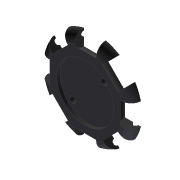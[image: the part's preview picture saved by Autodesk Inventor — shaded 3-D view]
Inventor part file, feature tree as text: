
AUTODESK INVENTOR PART (.ipt)
format: ipt  version: 2017 (Build 210142000, 142)  size: 216,576 bytes
history: native  units: mm
features: sketch x4, extrude x3, revolve x1, fillet x1, pattern_circular x1, hole x1, projected_geometry x1
ambient origin geometry x8: Origin, YZ Plane, XZ Plane, XY Plane, X Axis, Y Axis, Z Axis, Center Point
bodies: Solid1 (feature_tree)
feature tree (12):
  sketch  "Sketch1"  dims[d0=60.0mm d1=14.0mm]
  extrude  "Extrusion1"  Depth=14.0mm
  revolve  "Revolution1"  [1 undecoded]
  extrude  "Extrusion2"  Depth=1.75mm
  fillet  "Fillet1"  Radius=1.75mm
  pattern_circular  "Circular Pattern1"  [2 undecoded]
  hole  "Hole1"  [1 undecoded]
  extrude  "Extrusion3"  Depth=2.0mm TaperAngle=0.0deg
  sketch  "Sketch2"  dims[d2=7.0mm d3=19.0mm]
  projected_geometry  "Projected Loop1"
  sketch  "Sketch3"  dims[d4=5.0mm d5=5.0mm d6=1.75mm]
  sketch  "Sketch4"  dims[d7=1.75mm d8=6.0mm d9=0.0mm d10=90.0deg d11=12.0mm d12=0.0mm d13=6.0mm d14=80.0mm d15=360.0deg d17=45.0deg d18=180.0deg d19=14.0mm d20=14.0mm d21=4.0mm d22=6.0mm d23=4.0mm d24=2.0mm d25=90.0deg d26=8.0mm d27=20.594885mm d28=36.0mm d29=2.0mm d30=0.0mm]
note: 4 required parameter values undecoded (feature->parameter linkage not recoverable at this tier; creation-order binding heuristic only, values carry confidence <= 0.55)